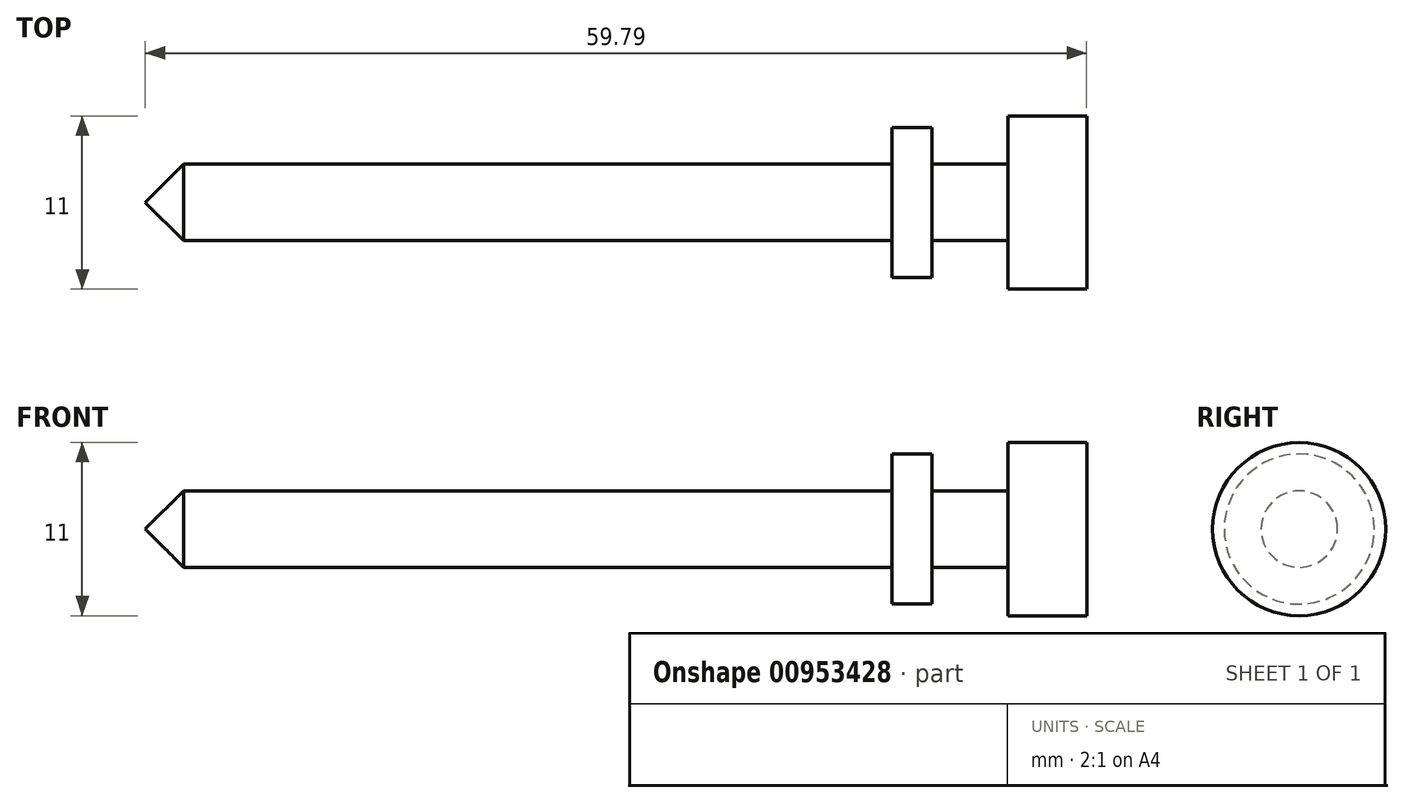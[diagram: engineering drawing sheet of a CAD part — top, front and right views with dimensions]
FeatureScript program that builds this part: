
annotation { "Feature Type Name" : "Feature", "Feature Type Description" : "" }
export const myFeature = defineFeature(function(context is Context, id is Id, definition is map)
    precondition{}
    {
        {
            var Q0;
            Q0=qCreatedBy(makeId("Front.planeOp"),FACE);
            var sketch = newSketch(context, id + "F0", { "sketchPlane" : qUnion([Q0])});
            skLineSegment(sketch, "E0", {"start": v(0, 0) * mm, "end": v(2.42, 2.43) * mm});
            skLineSegment(sketch, "E1", {"start": v(2.42, 2.43) * mm, "end": v(47.42, 2.43) * mm});
            skLineSegment(sketch, "E2", {"start": v(47.42, 2.43) * mm, "end": v(47.42, 4.76) * mm});
            skLineSegment(sketch, "E3", {"start": v(47.42, 4.76) * mm, "end": v(49.96, 4.76) * mm});
            skLineSegment(sketch, "E4", {"start": v(49.96, 4.76) * mm, "end": v(49.96, 2.43) * mm});
            skLineSegment(sketch, "E5", {"start": v(49.96, 2.43) * mm, "end": v(54.8, 2.43) * mm});
            skLineSegment(sketch, "E6", {"start": v(54.8, 2.43) * mm, "end": v(54.8, 5.5) * mm});
            skLineSegment(sketch, "E7", {"start": v(54.8, 5.5) * mm, "end": v(59.8, 5.5) * mm});
            skLineSegment(sketch, "E8", {"start": v(59.8, 5.5) * mm, "end": v(59.8, 0) * mm});
            skLineSegment(sketch, "E9.MirrorCS", {"start": v(54.8, -5.5) * mm, "end": v(59.8, -5.5) * mm});
            skLineSegment(sketch, "E10.MirrorCS", {"start": v(2.42, -2.43) * mm, "end": v(47.42, -2.43) * mm});
            skLineSegment(sketch, "E11.MirrorCS", {"start": v(49.96, -2.43) * mm, "end": v(54.8, -2.43) * mm});
            skLineSegment(sketch, "E12.MirrorCS", {"start": v(0, 0) * mm, "end": v(2.42, -2.43) * mm});
            skLineSegment(sketch, "E13.MirrorCS", {"start": v(49.96, -4.76) * mm, "end": v(49.96, -2.43) * mm});
            skLineSegment(sketch, "E14.MirrorCS", {"start": v(47.42, -4.76) * mm, "end": v(49.96, -4.76) * mm});
            skLineSegment(sketch, "E15.MirrorCS", {"start": v(59.8, -5.5) * mm, "end": v(59.8, 0) * mm});
            skLineSegment(sketch, "E16.MirrorCS", {"start": v(47.42, -2.43) * mm, "end": v(47.42, -4.76) * mm});
            skLineSegment(sketch, "E17.MirrorCS", {"start": v(54.8, -2.43) * mm, "end": v(54.8, -5.5) * mm});
            skLineSegment(sketch, "E18", {"start": v(59.8, 0) * mm, "end": v(0, 0) * mm});
            skSolve(sketch);
        }
        {
            var Q0;
            Q0=makeQuery(id+"F0.imprint","IMPRINT",FACE,{"disambiguationData":[TD([[makeQuery(id+"F0.imprint","IMPRINT",EDGE,{"derivedFrom":sQuery(id+"F0.wireOp",EDGE,"E0")}),-1.0]])]});
            var Q1;
            Q1=sQuery(id+"F0.wireOp",EDGE,"E18");
            revolve(context, id + "F1", {"surfaceOperationType" : NewSurfaceOperationType.NEW, "entities" : qUnion([Q0]), "axis" : qUnion([Q1]), "revolveType" : RevolveType.FULL});
        }
    });
